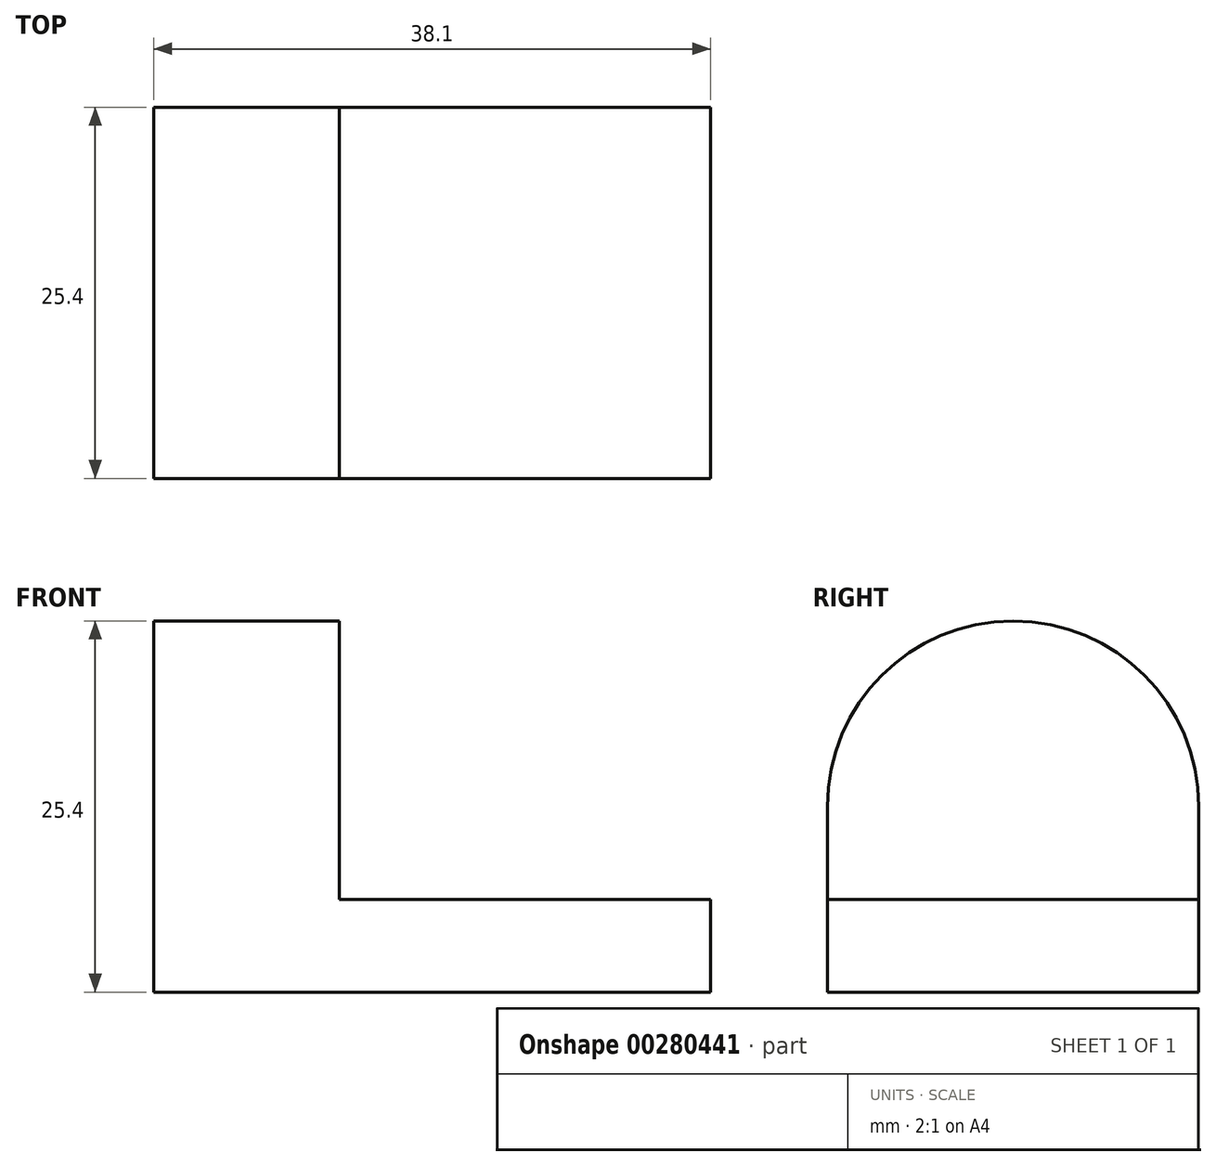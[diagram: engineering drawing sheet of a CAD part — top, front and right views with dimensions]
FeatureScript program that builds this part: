
annotation { "Feature Type Name" : "Feature", "Feature Type Description" : "" }
export const myFeature = defineFeature(function(context is Context, id is Id, definition is map)
    precondition{}
    {
        {
            var Q0;
            Q0=qCreatedBy(makeId("Right.planeOp"),FACE);
            var sketch = newSketch(context, id + "F0", { "sketchPlane" : qUnion([Q0])});
            skLineSegment(sketch, "E0", {"start": v(0, 12.7) * mm, "end": v(0, 0) * mm});
            skLineSegment(sketch, "E1", {"start": v(0, 0) * mm, "end": v(25.4, 0) * mm});
            skLineSegment(sketch, "E2", {"start": v(25.4, 0) * mm, "end": v(25.4, 12.7) * mm});
            skArc(sketch, "E3", {"start": v(25.4, 12.7) * mm, "mid": v(12.7, 25.4) * mm, "end": v(0, 12.7) * mm});
            skSolve(sketch);
        }
        {
            var Q0;
            Q0 = qSketchRegion(id + "F0", true);
            extrude(context, id + "F1", {"entities" : qUnion([Q0]), "oppositeDirection" : true, "depth" : 38.1 * mm});
        }
        {
            var Q0;
            Q0=qCreatedBy(makeId("Right.planeOp"),FACE);
            var sketch = newSketch(context, id + "F2", { "sketchPlane" : qUnion([Q0])});
            skLineSegment(sketch, "E4.bottom", {"start": v(0, 25.4) * mm, "end": v(25.4, 25.4) * mm});
            skLineSegment(sketch, "E4.top", {"start": v(0, 6.35) * mm, "end": v(25.4, 6.35) * mm});
            skLineSegment(sketch, "E4.left", {"start": v(0, 25.4) * mm, "end": v(0, 6.35) * mm});
            skLineSegment(sketch, "E4.right", {"start": v(25.4, 25.4) * mm, "end": v(25.4, 6.35) * mm});
            skSolve(sketch);
        }
        {
            var Q0;
            Q0 = qSketchRegion(id + "F2", true);
            extrude(context, id + "F3", {"entities" : qUnion([Q0]), "operationType" : NewBodyOperationType.REMOVE, "oppositeDirection" : true, "depth" : 25.4 * mm});
        }
    });
